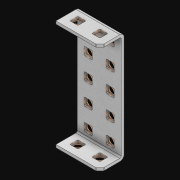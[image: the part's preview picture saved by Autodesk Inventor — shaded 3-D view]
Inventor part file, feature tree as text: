
AUTODESK INVENTOR PART (.ipt)
format: ipt  version: 2021 (Build 250183000, 183)  size: 2,754,560 bytes
history: native  units: in
note: dims shown in document units (in); Inventor stores cm internally (conversion verified against a paired STEP export)
features: extrude x15, other x14, sketch x4, thicken_offset x3, pattern_linear x3, imported_body x1
ambient origin geometry x8: Origin, YZ Plane, XZ Plane, XY Plane, X Axis, Y Axis, Z Axis, Center Point
bodies: Solid1 (feature_tree)
feature tree (40):
  thicken_offset  "Thicken1"
  thicken_offset  "Thicken2"
  thicken_offset  "Thicken3"
  pattern_linear  "Rectangular Pattern1"  Spacing1=0.001in  [1 undecoded]
  pattern_linear  "Rectangular Pattern2"  Spacing1=0.001in  [1 undecoded]
  pattern_linear  "Rectangular Pattern3"  Spacing1=0.182in  [1 undecoded]
  extrude  "Extrusion1"  Depth=0.063in TaperAngle=0.0deg
  sketch  "Sketch1"  dims[d0=0.001in]
  other  "Srf1"
  sketch  "Sketch2"  dims[d1=0.001in]
  other  "Srf2"
  sketch  "Sketch3"  dims[d2=0.001in]
  other  "Srf3"
  other  "Srf4"
  other  "Srf38"
  other  "Srf72"
  other  "Srf106"
  other  "Srf107"
  other  "Srf141"
  other  "Srf142"
  other  "Srf176"
  other  "Srf177"
  other  "Srf211"
  other  "Srf212"
  sketch  "Sketch4"  dims[d3=0.001in d4=0.001in d5=0.001in d6=0.182in d7=0.063in d8=0.0in d9=0.182in d10=0.063in d11=0.0in d12=0.182in d13=0.063in d14=0.0in d17=0.5in d18=0.7874in d20=0.5in d21=0.7874in d23=0.5in d24=1.9685in d26=0.5in d27=16.5in d28=0.0in]
  imported_body  "Imported1"
  extrude  "ExtrusionSrf1"  Depth=0.182in
  extrude  "ExtrusionSrf2"  Depth=0.063in TaperAngle=0.0deg
  extrude  "ExtrusionSrf3"  Depth=0.182in
  extrude  "ExtrusionSrf4"  Depth=0.063in TaperAngle=0.0deg
  extrude  "ExtrusionSrf38"  Depth=0.5in
  extrude  "ExtrusionSrf72"  Depth=0.5in
  extrude  "ExtrusionSrf106"  Depth=0.5in
  extrude  "ExtrusionSrf107"  Depth=0.5in
  extrude  "ExtrusionSrf141"  Depth=0.5in
  extrude  "ExtrusionSrf142"  Depth=0.5in
  extrude  "ExtrusionSrf176"  Depth=0.5in
  extrude  "ExtrusionSrf177"  TaperAngle=0.0deg  [1 undecoded]
  extrude  "ExtrusionSrf211"  [1 undecoded]
  extrude  "ExtrusionSrf212"  [1 undecoded]
note: 6 required parameter values undecoded (feature->parameter linkage not recoverable at this tier; creation-order binding heuristic only, values carry confidence <= 0.55)
